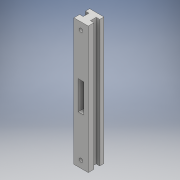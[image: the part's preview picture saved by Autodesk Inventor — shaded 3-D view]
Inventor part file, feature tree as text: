
AUTODESK INVENTOR PART (.ipt)
format: ipt  version: 2018 (Build 220112000, 112)  size: 168,960 bytes
history: native  units: mm
features: sketch x6, extrude x5, fillet x1, revolve x1
ambient origin geometry x8: Origin, YZ Plane, XZ Plane, XY Plane, X Axis, Y Axis, Z Axis, Center Point
bodies: Solid1 (feature_tree)
feature tree (13):
  extrude  "Extrusion1"  Depth=10.0mm
  extrude  "Extrusion2"  Depth=3.0mm
  extrude  "Extrusion3"  Depth=2.5mm
  extrude  "Extrusion4"  Depth=2.5mm
  extrude  "Extrusion5"  Depth=4.0mm TaperAngle=0.0deg
  fillet  "Fillet1"  Radius=4.0mm
  revolve  "Revolution1"  [1 undecoded]
  sketch  "Sketch1"  dims[d0=88.5mm d1=10.0mm]
  sketch  "Sketch2"  dims[d2=11.0mm d3=0.0mm d4=3.0mm]
  sketch  "Sketch3"  dims[d5=4.0mm d6=2.5mm]
  sketch  "Sketch4"  dims[d7=11.0mm d8=0.0mm d9=2.5mm]
  sketch  "Sketch5"  dims[d10=39.25mm d11=4.0mm d12=0.0mm d13=4.0mm]
  sketch  "Sketch7"  dims[d14=20.0mm d15=1.0mm d16=4.7mm d17=0.0mm d18=0.5mm d19=1.0mm d20=0.0mm d21=4.0mm d24=3.0mm d25=3.0mm d26=90.0deg]
note: 1 required parameter value undecoded (feature->parameter linkage not recoverable at this tier; creation-order binding heuristic only, values carry confidence <= 0.55)
